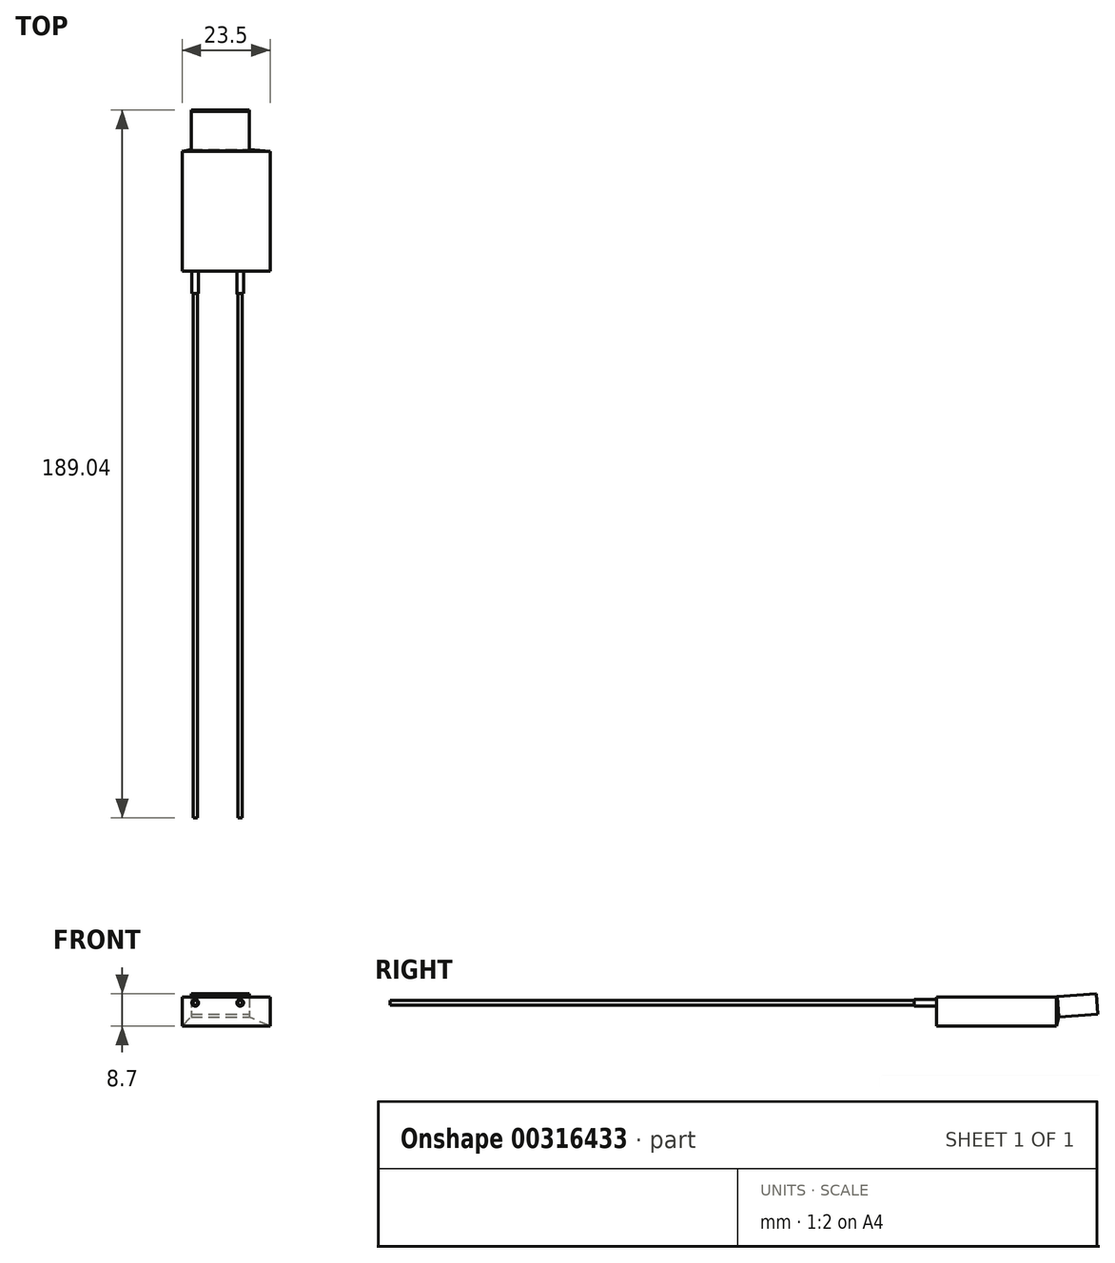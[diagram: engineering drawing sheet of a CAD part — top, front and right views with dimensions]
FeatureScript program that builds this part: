
annotation { "Feature Type Name" : "Feature", "Feature Type Description" : "" }
export const myFeature = defineFeature(function(context is Context, id is Id, definition is map)
    precondition{}
    {
        {
            var Q0;
            Q0=qCreatedBy(makeId("Top.planeOp"),FACE);
            var sketch = newSketch(context, id + "F0", { "sketchPlane" : qUnion([Q0])});
            skLineSegment(sketch, "E0.bottom", {"start": v(-11.75, 16) * mm, "end": v(11.75, 16) * mm});
            skLineSegment(sketch, "E0.top", {"start": v(-11.75, -16) * mm, "end": v(11.75, -16) * mm});
            skLineSegment(sketch, "E0.left", {"start": v(-11.75, 16) * mm, "end": v(-11.75, -16) * mm});
            skLineSegment(sketch, "E0.right", {"start": v(11.75, 16) * mm, "end": v(11.75, -16) * mm});
            skPoint(sketch, "E0.middle", {"position": v(0, 0) * mm});
            skSolve(sketch);
        }
        {
            var Q0;
            Q0 = qSketchRegion(id + "F0", true);
            extrude(context, id + "F1", {"entities" : qUnion([Q0]), "depth" : 7.75 * mm});
        }
        {
            var Q0;
            Q0=makeQuery(id+"F1.opExtrude","CAP_EDGE",EDGE,{"disambiguationData":[OSD([sQuery(id+"F0.wireOp",EDGE,"E0.bottom")])],"isStart":false});
            cPlane(context, id + "F2", {"entities" : qUnion([Q0]), "cplaneType" : CPlaneType.LINE_ANGLE, "offset" : 25 * mm, "angle" : 4 * degree, "width" : 150 * mm, "height" : 150 * mm});
        }
        {
            var Q0;
            Q0=qCreatedBy(id+"F2.planeOp",FACE);
            cPlane(context, id + "F3", {"entities" : qUnion([Q0]), "cplaneType" : CPlaneType.OFFSET, "offset" : 0.2 * mm, "width" : 150 * mm, "height" : 150 * mm});
        }
        {
            var Q0;
            Q0=qCreatedBy(id+"F3.planeOp",FACE);
            var sketch = newSketch(context, id + "F4", { "sketchPlane" : qUnion([Q0])});
            skLineSegment(sketch, "E1.bottom", {"start": v(9.35, 6.82) * mm, "end": v(-6.15, 6.82) * mm});
            skLineSegment(sketch, "E1.top", {"start": v(9.35, 1.32) * mm, "end": v(-6.15, 1.32) * mm});
            skLineSegment(sketch, "E1.left", {"start": v(9.35, 6.82) * mm, "end": v(9.35, 1.32) * mm});
            skLineSegment(sketch, "E1.right", {"start": v(-6.15, 6.82) * mm, "end": v(-6.15, 1.32) * mm});
            skSolve(sketch);
        }
        {
            var Q0;
            Q0 = qSketchRegion(id + "F4", true);
            extrude(context, id + "F5", {"entities" : qUnion([Q0]), "depth" : 10.5 * mm});
        }
        {
            var Q2;
            Q2=makeQuery(id+"F1.opExtrude","SWEPT_FACE",FACE,{"disambiguationData":[OSD([sQuery(id+"F0.wireOp",EDGE,"E0.bottom")])]});
            var Q3;
            Q3=makeQuery(id+"F5.opExtrude","CAP_FACE",FACE,{"disambiguationData":[OSD([sQuery(id+"F4.wireOp",EDGE,"E1.bottom"),sQuery(id+"F4.wireOp",EDGE,"E1.top"),sQuery(id+"F4.wireOp",EDGE,"E1.left"),sQuery(id+"F4.wireOp",EDGE,"E1.right")])],"isStart":true});
            loft(context, id + "F6", {"operationType" : NewBodyOperationType.ADD, "sheetProfilesArray" : [{ "sheetProfileEntities" : qUnion([Q2]) }, { "sheetProfileEntities" : qUnion([Q3]) }]});
        }
        {
            var Q0;
            Q0=makeQuery(id+"F1.opExtrude","SWEPT_FACE",FACE,{"disambiguationData":[OSD([sQuery(id+"F0.wireOp",EDGE,"E0.top")])]});
            var sketch = newSketch(context, id + "F7", { "sketchPlane" : qUnion([Q0])});
            skCircle(sketch, "E2", {"center": v(-8.25, 6.25) * mm, "radius": 0.9 * mm});
            skCircle(sketch, "E3", {"center": v(3.75, 6.25) * mm, "radius": 0.9 * mm});
            skSolve(sketch);
        }
        {
            var Q0;
            Q0 = qSketchRegion(id + "F7", true);
            extrude(context, id + "F8", {"entities" : qUnion([Q0]), "operationType" : NewBodyOperationType.ADD, "depth" : 6 * mm});
        }
        {
            var Q0;
            Q0=makeQuery(id+"F8.opExtrude","CAP_FACE",FACE,{"disambiguationData":[OSD([sQuery(id+"F7.wireOp",EDGE,"E2")])],"isStart":false});
            var sketch = newSketch(context, id + "F9", { "sketchPlane" : qUnion([Q0])});
            skCircle(sketch, "E4", {"center": v(-8.25, 6.25) * mm, "radius": 0.6 * mm});
            skCircle(sketch, "E5", {"center": v(3.75, 6.25) * mm, "radius": 0.6 * mm});
            skSolve(sketch);
        }
        {
            var Q0;
            Q0 = qSketchRegion(id + "F9", true);
            extrude(context, id + "F10", {"entities" : qUnion([Q0]), "operationType" : NewBodyOperationType.ADD, "depth" : 140 * mm});
        }
    });
